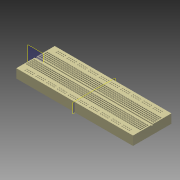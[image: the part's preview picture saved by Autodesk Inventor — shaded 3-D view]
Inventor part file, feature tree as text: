
AUTODESK INVENTOR PART (.ipt)
format: ipt  version: 2013 (Build 170138000, 138)  size: 5,305,344 bytes
history: native  units: in
note: dims shown in document units (in); Inventor stores cm internally (conversion verified against a paired STEP export)
features: sketch x6, extrude x5, pattern_linear x4, chamfer x3, plane x2, mirror x2, emboss x1, other x1
ambient origin geometry x8: Origin, YZ Plane, XZ Plane, XY Plane, X Axis, Y Axis, Z Axis, Center Point
bodies: Solid1 (feature_tree)
feature tree (24):
  extrude  "Extrusion1"  Depth=2.14in
  extrude  "Extrusion2"  Depth=0.5in TaperAngle=0.0deg
  sketch  "Sketch3"  dims[d17=0.1in d19=0.05in d20=0.0in]
  extrude  "Extrusion3"  Depth=0.05in TaperAngle=0.0deg
  plane  "Work Plane1"
  chamfer  "Chamfer1"  Distance=0.05in
  pattern_linear  "Rectangular Pattern1"  Spacing1=0.01in  [1 undecoded]
  extrude  "Extrusion4"  Depth=25.1969in
  chamfer  "Chamfer2"  Distance=1.9685in
  pattern_linear  "Rectangular Pattern2"  Spacing1=0.05in  [1 undecoded]
  plane  "Work Plane2"
  extrude  "Extrusion5"  Depth=0.01in TaperAngle=45.0deg
  chamfer  "Chamfer3"  Distance=25.1969in
  pattern_linear  "Rectangular Pattern3"  Count1=5 Spacing1=0.1in
  pattern_linear  "Rectangular Pattern4"  Spacing1=0.04in  [1 undecoded]
  mirror  "Mirror3"
  mirror  "Mirror4"
  emboss  "Emboss1"
  sketch  "Sketch6"  dims[d24=0.475in d25=0.05in d26=0.0in d27=0.01in d28=0.125in d29=45.0deg d30=25.1969in d32=0.1in d33=1.9685in d35=0.1in d36=0.05in d37=0.0in d38=0.01in d39=0.125in d40=45.0deg d41=25.1969in d43=0.1in d44=1.9685in d46=0.1in d47=0.04in d50=0.135in d51=0.075in d52=0.075in d53=0.05in d54=0.0in d55=0.01in d56=0.125in d57=45.0deg d58=1.9685in d60=0.1in d61=0.7874in d63=0.1in d64=1.9685in d66=0.6in d67=0.05in d68=0.0in]
  sketch  "Sketch1"  dims[d10=6.496in d11=2.14in]
  other  "Image1"
  sketch  "Sketch2"  dims[d14=2.14in d15=0.5in d16=0.0in]
  sketch  "Sketch4"  dims[d21=0.065in]
  sketch  "Sketch5"  dims[d23=0.0655in]
note: 3 required parameter values undecoded (feature->parameter linkage not recoverable at this tier; creation-order binding heuristic only, values carry confidence <= 0.55)
